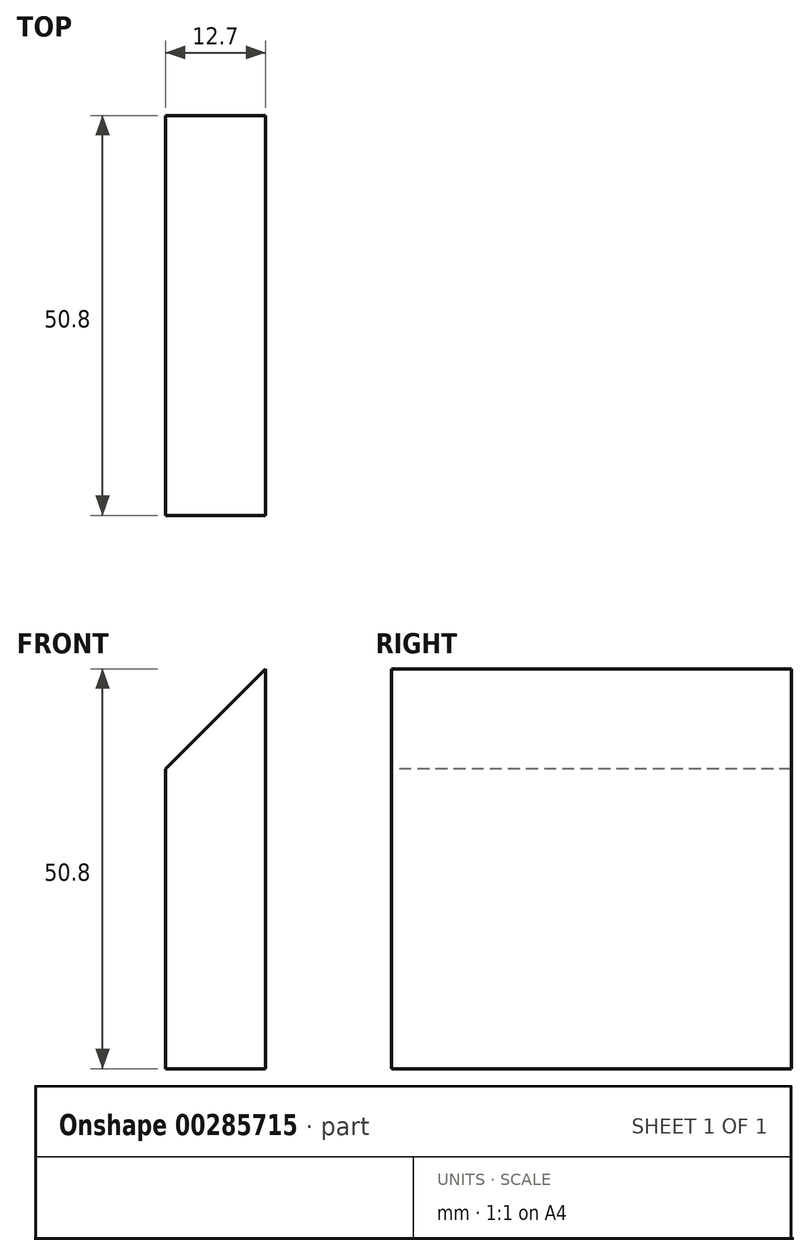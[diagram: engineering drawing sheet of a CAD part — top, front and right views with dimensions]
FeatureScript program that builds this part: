
annotation { "Feature Type Name" : "Feature", "Feature Type Description" : "" }
export const myFeature = defineFeature(function(context is Context, id is Id, definition is map)
    precondition{}
    {
        {
            var Q0;
            Q0=qCreatedBy(makeId("Right.planeOp"),FACE);
            var sketch = newSketch(context, id + "F0", { "sketchPlane" : qUnion([Q0])});
            skLineSegment(sketch, "E0.bottom", {"start": v(0, 0) * mm, "end": v(50.8, 0) * mm});
            skLineSegment(sketch, "E0.top", {"start": v(0, 50.8) * mm, "end": v(50.8, 50.8) * mm});
            skLineSegment(sketch, "E0.left", {"start": v(0, 0) * mm, "end": v(0, 50.8) * mm});
            skLineSegment(sketch, "E0.right", {"start": v(50.8, 0) * mm, "end": v(50.8, 50.8) * mm});
            skSolve(sketch);
        }
        {
            var Q0;
            Q0 = qSketchRegion(id + "F0", true);
            extrude(context, id + "F1", {"entities" : qUnion([Q0]), "depth" : 12.7 * mm});
        }
        {
            var Q0;
            Q0=makeQuery(id+"F1.opExtrude","SWEPT_FACE",FACE,{"disambiguationData":[OSD([sQuery(id+"F0.wireOp",EDGE,"E0.left")])]});
            var sketch = newSketch(context, id + "F2", { "sketchPlane" : qUnion([Q0])});
            skLineSegment(sketch, "E1", {"start": v(0, 38.1) * mm, "end": v(12.7, 50.8) * mm});
            skLineSegment(sketch, "E2", {"start": v(12.7, 50.8) * mm, "end": v(0, 50.8) * mm});
            skLineSegment(sketch, "E3", {"start": v(0, 38.1) * mm, "end": v(0, 50.8) * mm});
            skSolve(sketch);
        }
        {
            var Q0;
            Q0 = qSketchRegion(id + "F2", true);
            extrude(context, id + "F3", {"entities" : qUnion([Q0]), "operationType" : NewBodyOperationType.REMOVE, "oppositeDirection" : true, "depth" : 50.8 * mm});
        }
    });
